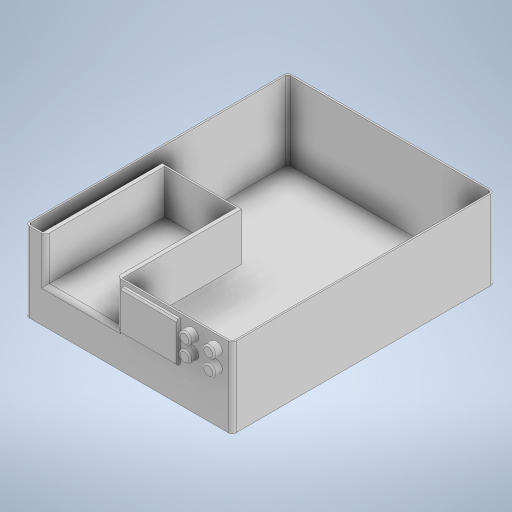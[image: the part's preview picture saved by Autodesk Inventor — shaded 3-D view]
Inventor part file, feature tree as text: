
AUTODESK INVENTOR PART (.ipt)
format: ipt  version: 2023 (Build 270158000, 158)  size: 330,752 bytes
history: native  units: mm
features: extrude x5, sketch x5, fillet x3, projected_geometry x3, shell x1, chamfer x1
ambient origin geometry x8: Origin, YZ Plane, XZ Plane, XY Plane, X Axis, Y Axis, Z Axis, Center Point
bodies: Solid1 (feature_tree)
feature tree (18):
  extrude  "Extrusion1"  Depth=330.0mm
  fillet  "Fillet1"  Radius=100.0mm
  shell  "Shell1"  Thickness=2.0mm
  extrude  "Extrusion3"  Depth=100.0mm
  extrude  "Extrusion4"  Depth=150.0mm
  fillet  "Fillet3"  Radius=150.0mm
  extrude  "Extrusion5"  Depth=5.0mm
  fillet  "Fillet4"  Radius=5.0mm
  extrude  "Extrusion6"  Depth=5.0mm
  chamfer  "Chamfer1"  Distance=15.0mm
  sketch  "Sketch1"  dims[d0=260.0mm d1=330.0mm d2=100.0mm d3=0.0mm d10=2.0mm]
  sketch  "Sketch3"  dims[d11=5.0mm d13=100.0mm]
  sketch  "Sketch4"  dims[d14=60.0mm d15=15.0mm d16=150.0mm d17=0.0mm]
  projected_geometry  "Projected Loop1"
  projected_geometry  "Projected Loop2"
  projected_geometry  "Projected Loop3"
  sketch  "Sketch5"  dims[d18=5.0mm d19=5.0mm d20=5.0mm]
  sketch  "Sketch6"  dims[d21=150.0mm d22=0.0mm d23=5.0mm d24=15.0mm d25=15.0mm d26=15.0mm d27=20.0mm d29=30.0mm d30=20.0mm d32=20.0mm d35=10.0mm d36=0.0mm d37=2.0mm d38=5.0mm d39=5.0mm d40=70.0mm d41=50.0mm d42=5.0mm d43=0.0mm d44=2.0mm d45=2.0mm d46=45.0deg d47=0.872665mm]
